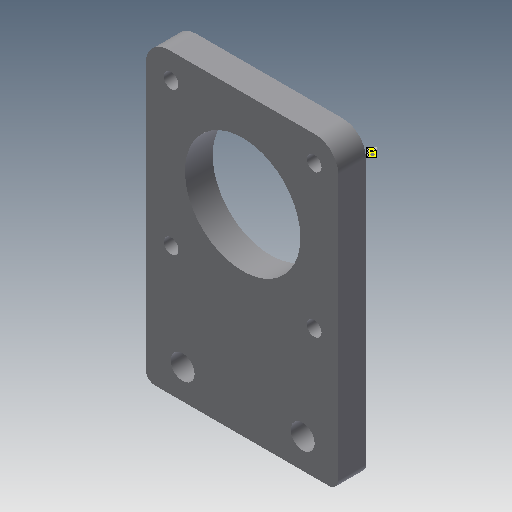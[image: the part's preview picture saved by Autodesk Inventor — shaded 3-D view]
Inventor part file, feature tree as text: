
AUTODESK INVENTOR PART (.ipt)
format: ipt  version: 2017 (Build 210142000, 142)  size: 161,280 bytes
history: native  units: mm
features: sketch x3, extrude x1
ambient origin geometry x8: Origin, YZ Plane, XZ Plane, XY Plane, X Axis, Y Axis, Z Axis, Center Point
bodies: Solid1 (feature_tree)
feature tree (4):
  sketch  "Sketch1"  dims[d8=3.2mm d9=3.2mm]
  sketch  "Sketch2"  dims[d10=5.5mm]
  sketch  "Sketch3"  dims[d13=5.2mm d14=5.2mm d16=2.0mm d17=40.0mm d18=90.0deg d19=20.0mm d22=20.0mm d23=10.0mm d24=8.5mm d25=6.0mm d26=0.0mm d27=2.0mm]
  extrude  "Extrusion1"  Depth=3.2mm
